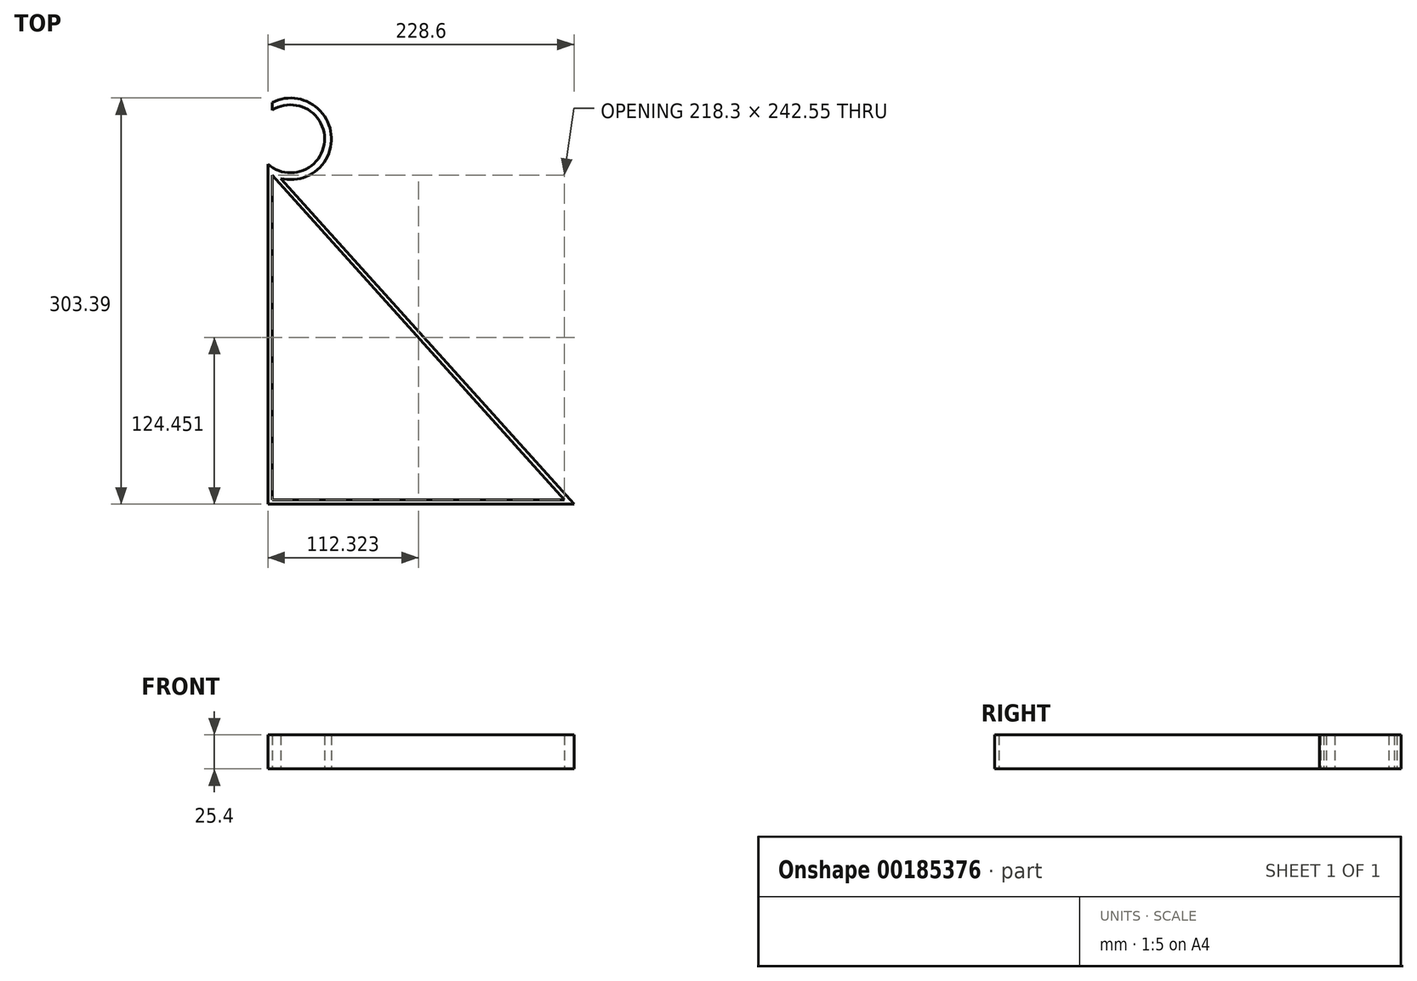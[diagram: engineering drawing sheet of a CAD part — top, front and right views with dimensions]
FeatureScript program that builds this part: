
annotation { "Feature Type Name" : "Feature", "Feature Type Description" : "" }
export const myFeature = defineFeature(function(context is Context, id is Id, definition is map)
    precondition{}
    {
        {
            var Q0;
            Q0=qCreatedBy(makeId("Top.planeOp"),FACE);
            var sketch = newSketch(context, id + "F0", { "sketchPlane" : qUnion([Q0])});
            skLineSegment(sketch, "E0", {"start": v(0, 0) * mm, "end": v(0, 254) * mm});
            skLineSegment(sketch, "E1", {"start": v(0, 0) * mm, "end": v(228.6, 0) * mm});
            skLineSegment(sketch, "E2", {"start": v(9.6, 243.33) * mm, "end": v(228.6, 0) * mm});
            skLineSegment(sketch, "E3", {"start": v(3.18, 3.17) * mm, "end": v(3.18, 245.73) * mm});
            skLineSegment(sketch, "E4", {"start": v(3.17, 3.18) * mm, "end": v(221.47, 3.18) * mm});
            skLineSegment(sketch, "E5", {"start": v(221.47, 3.17) * mm, "end": v(3.17, 245.73) * mm});
            skArc(sketch, "E6", {"start": v(9.6, 243.33) * mm, "mid": v(47.24, 276.34) * mm, "end": v(3.17, 300.1) * mm});
            skArc(sketch, "E7", {"start": v(0, 254) * mm, "mid": v(42.27, 270.92) * mm, "end": v(3.18, 294.25) * mm});
            skLineSegment(sketch, "E8", {"start": v(3.17, 300.1) * mm, "end": v(3.17, 294.25) * mm});
            skSolve(sketch);
        }
        {
            var Q0;
            Q0=makeQuery(id+"F0.imprint","IMPRINT",FACE,{"disambiguationData":[TD([[makeQuery(id+"F0.imprint","IMPRINT",EDGE,{"derivedFrom":sQuery(id+"F0.wireOp",EDGE,"E0")}),-1.0]])]});
            extrude(context, id + "F1", {"entities" : qUnion([Q0]), "depth" : 25.4 * mm});
        }
    });
